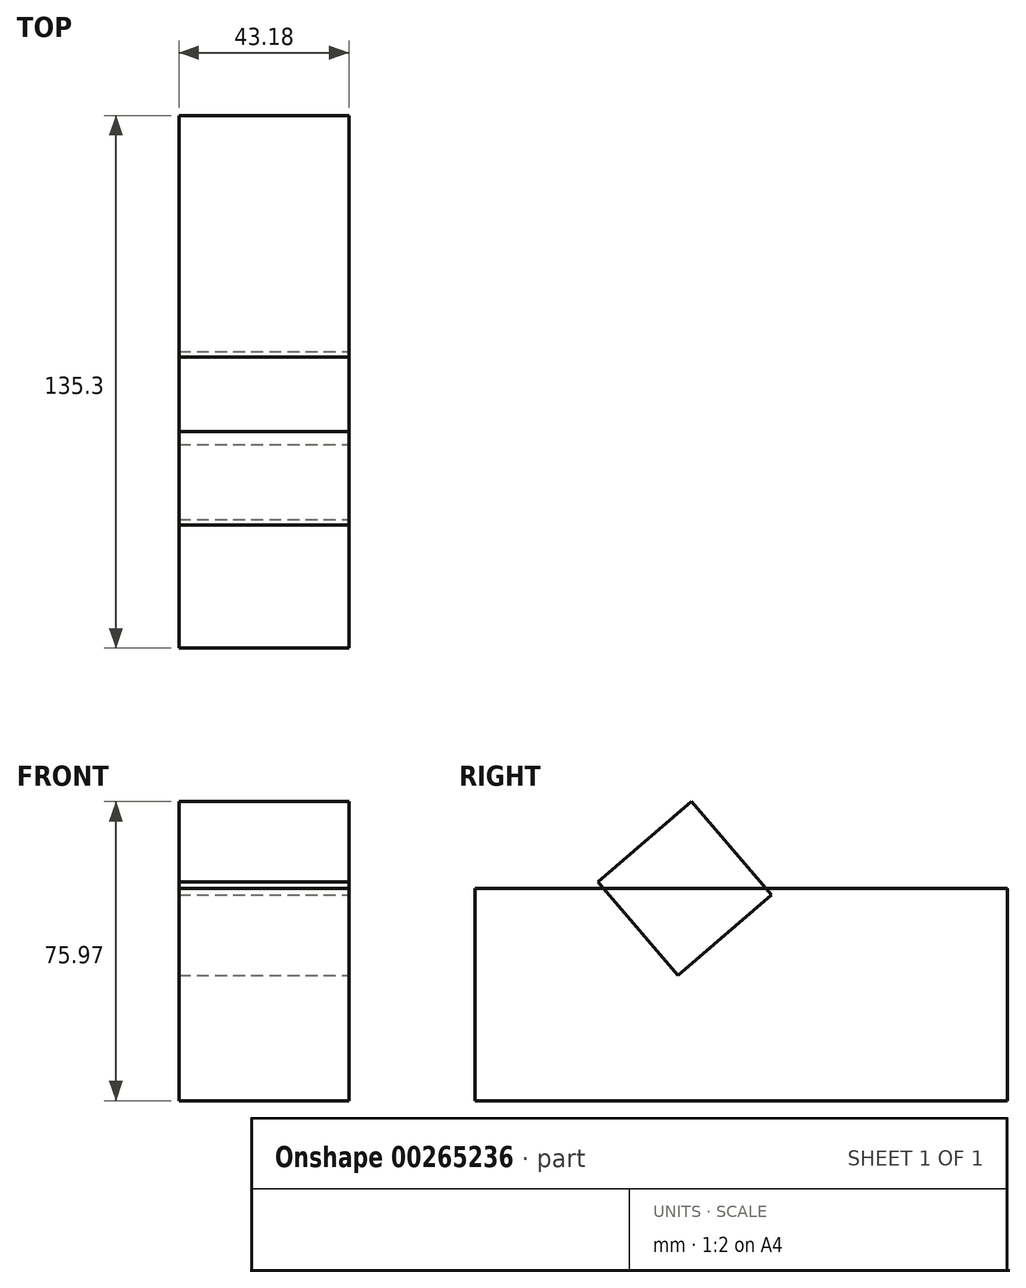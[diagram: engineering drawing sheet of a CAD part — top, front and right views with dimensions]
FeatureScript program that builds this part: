
annotation { "Feature Type Name" : "Feature", "Feature Type Description" : "" }
export const myFeature = defineFeature(function(context is Context, id is Id, definition is map)
    precondition{}
    {
        {
            var Q0;
            Q0=qCreatedBy(makeId("Right.planeOp"),FACE);
            var sketch = newSketch(context, id + "F0", { "sketchPlane" : qUnion([Q0])});
            skLineSegment(sketch, "E0.bottom", {"start": v(-74.07, 60.13) * mm, "end": v(61.23, 60.13) * mm});
            skLineSegment(sketch, "E0.top", {"start": v(-74.07, 6.2) * mm, "end": v(61.23, 6.2) * mm});
            skLineSegment(sketch, "E0.left", {"start": v(-74.07, 60.13) * mm, "end": v(-74.07, 6.2) * mm});
            skLineSegment(sketch, "E0.right", {"start": v(61.23, 60.13) * mm, "end": v(61.23, 6.2) * mm});
            skLineSegment(sketch, "E1.bottom", {"start": v(-74.07, 60.13) * mm, "end": v(-20.74, 60.13) * mm});
            skLineSegment(sketch, "E1.top", {"start": v(-74.07, 60.13) * mm, "end": v(-20.74, 60.13) * mm});
            skLineSegment(sketch, "E1.left", {"start": v(-74.07, 60.13) * mm, "end": v(-74.07, 60.13) * mm});
            skLineSegment(sketch, "E1.right", {"start": v(-20.74, 60.13) * mm, "end": v(-20.74, 60.13) * mm});
            skCircle(sketch, "E2.cCircle", {"center": v(-20.74, 60.13) * mm, "radius": 15.63 * mm, "construction": true});
            skLineSegment(sketch, "E2.0", {"start": v(-22.4, 38.08) * mm, "end": v(-42.78, 61.79) * mm});
            skLineSegment(sketch, "E2.1", {"start": v(-42.78, 61.79) * mm, "end": v(-19.08, 82.17) * mm});
            skLineSegment(sketch, "E2.2", {"start": v(-19.08, 82.17) * mm, "end": v(1.3, 58.47) * mm});
            skLineSegment(sketch, "E2.3", {"start": v(1.3, 58.47) * mm, "end": v(-22.4, 38.08) * mm});
            skPoint(sketch, "E2.0.midPoint", {"position": v(-32.59, 49.93) * mm});
            skSolve(sketch);
        }
        {
            var Q0;
            Q0=makeQuery(id+"F0.imprint","IMPRINT",FACE,{"disambiguationData":[TD([[makeQuery(id+"F0.imprint","IMPRINT",EDGE,{"derivedFrom":sQuery(id+"F0.wireOp",EDGE,"E0.top")}),1.0]])]});
            var Q1;
            {var subQ0=sQuery(id+"F0.wireOp",EDGE,"E2.1");Q1=makeQuery(id+"F0.imprint","IMPRINT",FACE,{"disambiguationData":[TD([[makeQuery(id+"F0.imprint","IMPRINT",EDGE,{"derivedFrom":subQ0}),-1.0]])]});}
            extrude(context, id + "F1", {"entities" : qUnion([Q0, Q1]), "oppositeDirection" : true, "depth" : 43.18 * mm});
        }
    });
